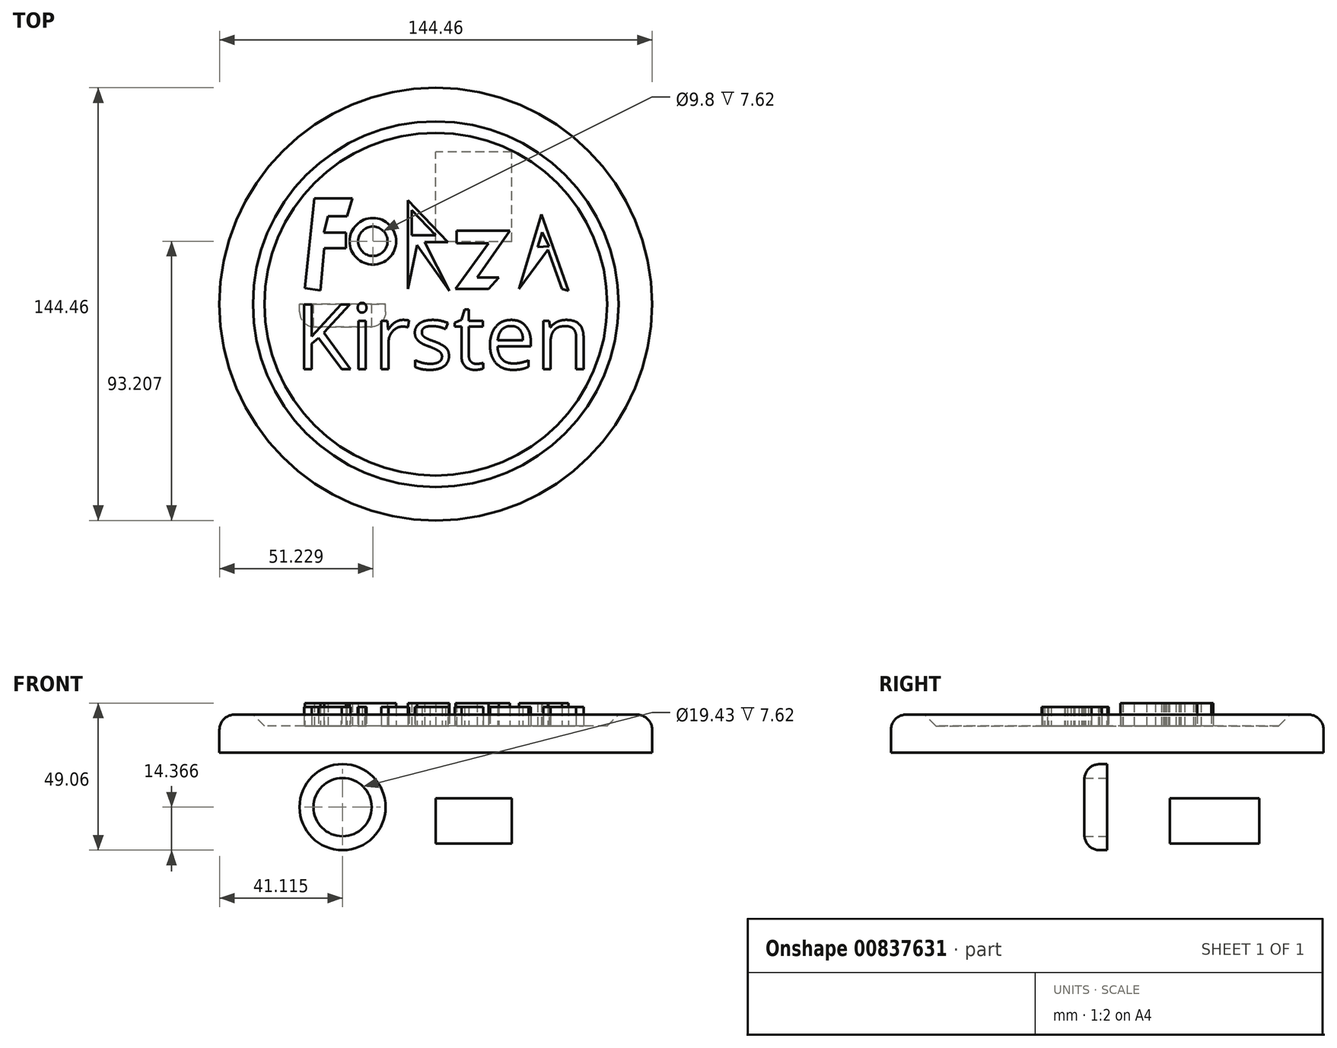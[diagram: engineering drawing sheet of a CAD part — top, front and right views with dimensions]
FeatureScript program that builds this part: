
annotation { "Feature Type Name" : "Feature", "Feature Type Description" : "" }
export const myFeature = defineFeature(function(context is Context, id is Id, definition is map)
    precondition{}
    {
        {
            var Q0;
            Q0=qCreatedBy(makeId("Top.planeOp"),FACE);
            var sketch = newSketch(context, id + "F0", { "sketchPlane" : qUnion([Q0])});
            skCircle(sketch, "E0", {"center": v(0, 0) * mm, "radius": 55.94 * mm});
            skCircle(sketch, "E1", {"center": v(0, 0) * mm, "radius": 72.23 * mm});
            skSolve(sketch);
        }
        {
            var Q0;
            Q0=makeQuery(id+"F0.imprint","IMPRINT",FACE,{"disambiguationData":[TD([[makeQuery(id+"F0.imprint","IMPRINT",EDGE,{"derivedFrom":sQuery(id+"F0.wireOp",EDGE,"E0")}),1.0]])]});
            extrude(context, id + "F1", {"entities" : qUnion([Q0]), "depth" : 8.9 * mm, "offsetDistance" : 25.4 * mm});
        }
        {
            var Q0;
            Q0 = qSketchRegion(id + "F0", true);
            extrude(context, id + "F2", {"entities" : qUnion([Q0]), "operationType" : NewBodyOperationType.ADD, "depth" : 12.7 * mm, "offsetDistance" : 25.4 * mm});
        }
        {
            var Q0;
            Q0=makeQuery(id+"F2.opExtrude","CAP_EDGE",EDGE,{"disambiguationData":[OSD([sQuery(id+"F0.wireOp",EDGE,"E0")])],"isStart":false});
            chamfer(context, id + "F3", {"entities" : qUnion([Q0]), "width" : 5.08 * mm, "tangentPropagation" : true});
        }
        {
            var Q0;
            Q0=makeQuery(id+"F2.opExtrude","CAP_EDGE",EDGE,{"disambiguationData":[OSD([sQuery(id+"F0.wireOp",EDGE,"E1")])],"isStart":false});
            fillet(context, id + "F4", {"entities" : qUnion([Q0]), "radius" : 5.08 * mm, "tangentPropagation" : true, "allowEdgeOverflow" : false});
        }
        {
            var Q0;
            Q0=makeQuery(id+"F1.opExtrude","CAP_FACE",FACE,{"disambiguationData":[OSD([sQuery(id+"F0.wireOp",EDGE,"E0")])],"isStart":false});
            var sketch = newSketch(context, id + "F5", { "sketchPlane" : qUnion([Q0])});
            skLineSegment(sketch, "E2", {"start": v(-43.77, 5.35) * mm, "end": v(-40.48, 35.36) * mm});
            skLineSegment(sketch, "E3", {"start": v(-40.48, 35.36) * mm, "end": v(-27.8, 35.36) * mm});
            skLineSegment(sketch, "E4", {"start": v(-27.8, 35.36) * mm, "end": v(-29.6, 29.36) * mm});
            skLineSegment(sketch, "E5", {"start": v(-29.6, 29.36) * mm, "end": v(-35.95, 29.36) * mm});
            skLineSegment(sketch, "E6", {"start": v(-35.95, 29.36) * mm, "end": v(-37.31, 23.92) * mm});
            skLineSegment(sketch, "E7", {"start": v(-37.31, 23.92) * mm, "end": v(-29.95, 23.92) * mm});
            skLineSegment(sketch, "E8", {"start": v(-29.95, 23.92) * mm, "end": v(-29.95, 18.71) * mm});
            skLineSegment(sketch, "E9", {"start": v(-29.95, 18.71) * mm, "end": v(-37.2, 18.71) * mm});
            skLineSegment(sketch, "E10", {"start": v(-37.2, 18.71) * mm, "end": v(-38.56, 4.55) * mm});
            skLineSegment(sketch, "E11", {"start": v(-38.56, 4.55) * mm, "end": v(-43.77, 5.35) * mm});
            skCircle(sketch, "E12", {"center": v(-21, 20.98) * mm, "radius": 7.77 * mm});
            skCircle(sketch, "E13", {"center": v(-21, 20.98) * mm, "radius": 4.9 * mm});
            skLineSegment(sketch, "E14", {"start": v(-9.33, 5.13) * mm, "end": v(-9.33, 34.7) * mm});
            skLineSegment(sketch, "E15", {"start": v(-9.33, 34.7) * mm, "end": v(4.03, 20.76) * mm});
            skLineSegment(sketch, "E16", {"start": v(4.03, 20.76) * mm, "end": v(-3.67, 20.76) * mm});
            skLineSegment(sketch, "E17", {"start": v(-3.67, 20.76) * mm, "end": v(4.49, 4.45) * mm});
            skLineSegment(sketch, "E18", {"start": v(4.49, 4.45) * mm, "end": v(-6.27, 19.75) * mm});
            skLineSegment(sketch, "E19", {"start": v(-6.27, 19.75) * mm, "end": v(-9.33, 5.13) * mm});
            skLineSegment(sketch, "E20", {"start": v(17.67, 5.13) * mm, "end": v(6.62, 5.13) * mm});
            skLineSegment(sketch, "E21", {"start": v(6.62, 5.13) * mm, "end": v(17.67, 20.35) * mm});
            skLineSegment(sketch, "E22", {"start": v(17.67, 20.35) * mm, "end": v(7, 20.35) * mm});
            skLineSegment(sketch, "E23", {"start": v(7, 20.35) * mm, "end": v(7, 24.54) * mm});
            skLineSegment(sketch, "E24", {"start": v(7, 24.54) * mm, "end": v(24.71, 24.54) * mm});
            skLineSegment(sketch, "E25", {"start": v(24.71, 24.54) * mm, "end": v(13.86, 8.92) * mm});
            skLineSegment(sketch, "E26", {"start": v(13.86, 8.92) * mm, "end": v(21.1, 8.92) * mm});
            skLineSegment(sketch, "E27", {"start": v(21.1, 8.92) * mm, "end": v(17.67, 5.13) * mm});
            skLineSegment(sketch, "E28", {"start": v(27.76, 5.13) * mm, "end": v(35.27, 30) * mm});
            skLineSegment(sketch, "E29", {"start": v(35.27, 30) * mm, "end": v(44.33, 4.45) * mm});
            skLineSegment(sketch, "E30", {"start": v(44.33, 4.45) * mm, "end": v(42.08, 5.13) * mm});
            skLineSegment(sketch, "E31", {"start": v(42.08, 5.13) * mm, "end": v(37.47, 18.13) * mm});
            skLineSegment(sketch, "E32", {"start": v(37.47, 18.13) * mm, "end": v(27.76, 5.13) * mm});
            skLineSegment(sketch, "E33", {"start": v(34, 19.07) * mm, "end": v(35.49, 24.03) * mm});
            skLineSegment(sketch, "E34", {"start": v(35.49, 24.03) * mm, "end": v(37.82, 19.37) * mm});
            skLineSegment(sketch, "E35", {"start": v(37.82, 19.37) * mm, "end": v(34, 19.07) * mm});
            skLineSegment(sketch, "E36", {"start": v(-8.03, 31.31) * mm, "end": v(-8.03, 22.98) * mm});
            skLineSegment(sketch, "E37", {"start": v(-8.03, 22.98) * mm, "end": v(0, 22.98) * mm});
            skLineSegment(sketch, "E38", {"start": v(0, 22.98) * mm, "end": v(-8.03, 31.31) * mm});
            skSolve(sketch);
        }
        {
            var Q0;
            Q0=makeQuery(id+"F5.imprint","IMPRINT",FACE,{"disambiguationData":[TD([[makeQuery(id+"F5.imprint","IMPRINT",EDGE,{"derivedFrom":sQuery(id+"F5.wireOp",EDGE,"E2")}),-1.0]])]});
            var Q1;
            Q1=makeQuery(id+"F5.imprint","IMPRINT",FACE,{"disambiguationData":[TD([[makeQuery(id+"F5.imprint","IMPRINT",EDGE,{"derivedFrom":sQuery(id+"F5.wireOp",EDGE,"E12")}),1.0]])]});
            var Q2;
            Q2=makeQuery(id+"F5.imprint","IMPRINT",FACE,{"disambiguationData":[TD([[makeQuery(id+"F5.imprint","IMPRINT",EDGE,{"derivedFrom":sQuery(id+"F5.wireOp",EDGE,"E14")}),-1.0]])]});
            var Q3;
            Q3=makeQuery(id+"F5.imprint","IMPRINT",FACE,{"disambiguationData":[TD([[makeQuery(id+"F5.imprint","IMPRINT",EDGE,{"derivedFrom":sQuery(id+"F5.wireOp",EDGE,"E20")}),-1.0]])]});
            var Q4;
            Q4=makeQuery(id+"F5.imprint","IMPRINT",FACE,{"disambiguationData":[TD([[makeQuery(id+"F5.imprint","IMPRINT",EDGE,{"derivedFrom":sQuery(id+"F5.wireOp",EDGE,"E28")}),-1.0]])]});
            extrude(context, id + "F6", {"entities" : qUnion([Q0, Q1, Q2, Q3, Q4]), "operationType" : NewBodyOperationType.ADD, "depth" : 7.62 * mm, "offsetDistance" : 25.4 * mm});
        }
        {
            var Q0;
            {var subQ0=sQuery(id+"F0.wireOp",EDGE,"E0");Q0=makeQuery(id+"F6.boolean.opBoolean","SPLIT",FACE,{"disambiguationData":[TD([makeQuery(id+"F3.opChamfer","BLEND_FACE",FACE,{"disambiguationData":[OSD([subQ0])]})])],"derivedFrom":makeQuery(id+"F1.opExtrude","CAP_FACE",FACE,{"disambiguationData":[OSD([subQ0])],"isStart":false})});}
            var sketch = newSketch(context, id + "F7", { "sketchPlane" : qUnion([Q0])});
            skText(sketch, "E39", { "text": "Kirsten", "fontName": "OpenSans-Regular.ttf"});
            const initialGuessF7  = {"E39": [-0.04688, -0.02165, 1, 0, 0.02165]};
            skSetInitialGuess(sketch, initialGuessF7);
            skSolve(sketch);
        }
        {
            var Q0;
            Q0 = qSketchRegion(id + "F7", true);
            extrude(context, id + "F8", {"entities" : qUnion([Q0]), "operationType" : NewBodyOperationType.ADD, "depth" : 6.35 * mm, "offsetDistance" : 25.4 * mm});
        }
        {
            var Q0;
            Q0=qCreatedBy(makeId("Front.planeOp"),FACE);
            var sketch = newSketch(context, id + "F9", { "sketchPlane" : qUnion([Q0])});
            skCircle(sketch, "E40", {"center": v(-31.12, -18.18) * mm, "radius": 14.36 * mm});
            skCircle(sketch, "E41", {"center": v(-31.12, -18.18) * mm, "radius": 9.71 * mm});
            skSolve(sketch);
        }
        {
            var Q0;
            Q0=makeQuery(id+"F9.imprint","IMPRINT",FACE,{"disambiguationData":[TD([[makeQuery(id+"F9.imprint","IMPRINT",EDGE,{"derivedFrom":sQuery(id+"F9.wireOp",EDGE,"E40")}),1.0]])]});
            extrude(context, id + "F10", {"entities" : qUnion([Q0]), "depth" : 7.62 * mm, "offsetDistance" : 25.4 * mm});
        }
        {
            var Q0;
            Q0=makeQuery(id+"F10.opExtrude","CAP_EDGE",EDGE,{"disambiguationData":[OSD([sQuery(id+"F9.wireOp",EDGE,"E40")])],"isStart":false});
            fillet(context, id + "F11", {"entities" : qUnion([Q0]), "radius" : 5.08 * mm, "tangentPropagation" : true, "allowEdgeOverflow" : false});
        }
        {
            var Q0;
            Q0=qCreatedBy(makeId("Right.planeOp"),FACE);
            var sketch = newSketch(context, id + "F12", { "sketchPlane" : qUnion([Q0])});
            skLineSegment(sketch, "E42.bottom", {"start": v(20.88, -15.22) * mm, "end": v(50.78, -15.22) * mm});
            skLineSegment(sketch, "E42.top", {"start": v(20.88, -30.3) * mm, "end": v(50.78, -30.3) * mm});
            skLineSegment(sketch, "E42.left", {"start": v(20.88, -15.22) * mm, "end": v(20.88, -30.3) * mm});
            skLineSegment(sketch, "E42.right", {"start": v(50.78, -15.22) * mm, "end": v(50.78, -30.3) * mm});
            skSolve(sketch);
        }
        {
            var Q0;
            Q0=makeQuery(id+"F12.imprint","IMPRINT",FACE,{"disambiguationData":[TD([[makeQuery(id+"F12.imprint","IMPRINT",EDGE,{"derivedFrom":sQuery(id+"F12.wireOp",EDGE,"E42.bottom")}),-1.0]])]});
            extrude(context, id + "F13", {"entities" : qUnion([Q0]), "depth" : 25.4 * mm, "offsetDistance" : 25.4 * mm});
        }
    });
